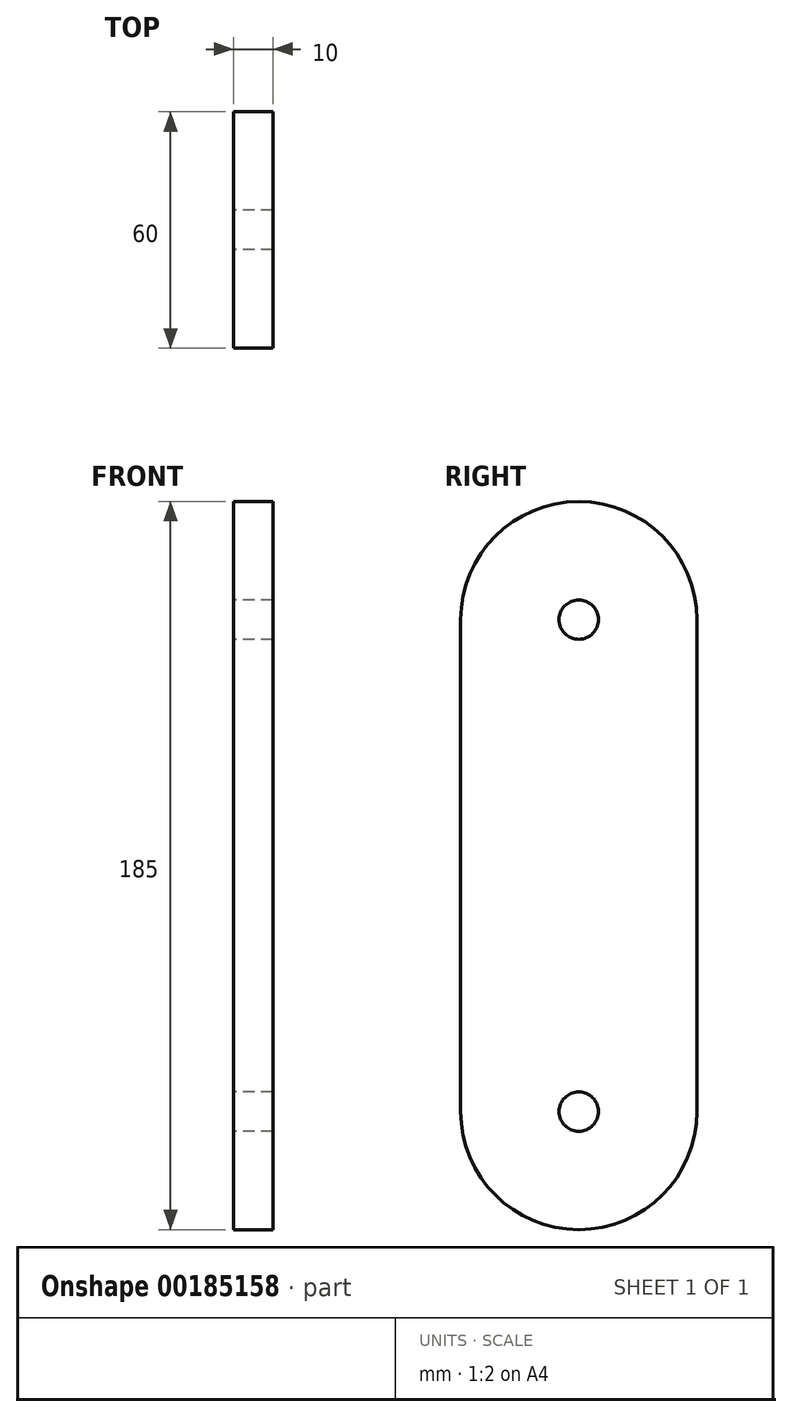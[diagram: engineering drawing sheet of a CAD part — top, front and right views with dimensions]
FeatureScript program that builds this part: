
annotation { "Feature Type Name" : "Feature", "Feature Type Description" : "" }
export const myFeature = defineFeature(function(context is Context, id is Id, definition is map)
    precondition{}
    {
        {
            var Q0;
            Q0=qCreatedBy(makeId("Right.planeOp"),FACE);
            var sketch = newSketch(context, id + "F0", { "sketchPlane" : qUnion([Q0])});
            skCircle(sketch, "E0", {"center": v(0, 0) * mm, "radius": 5 * mm});
            skArc(sketch, "E1", {"start": v(-30, 0) * mm, "mid": v(0, -30) * mm, "end": v(30, 0) * mm});
            skLineSegment(sketch, "E2", {"start": v(0, 0) * mm, "end": v(5, 0) * mm});
            skLineSegment(sketch, "E3", {"start": v(-30, 0) * mm, "end": v(-30, 125) * mm});
            skLineSegment(sketch, "E4", {"start": v(30, 0) * mm, "end": v(30, 125) * mm});
            skCircle(sketch, "E5", {"center": v(0, 125) * mm, "radius": 5 * mm});
            skArc(sketch, "E6", {"start": v(30, 125) * mm, "mid": v(0, 155) * mm, "end": v(-30, 125) * mm});
            skLineSegment(sketch, "E7", {"start": v(0, 0) * mm, "end": v(30, 0) * mm});
            skLineSegment(sketch, "E8", {"start": v(0, 125) * mm, "end": v(30, 125) * mm});
            skLineSegment(sketch, "E9", {"start": v(-30, 125) * mm, "end": v(30, 125) * mm});
            skSolve(sketch);
        }
        {
            var Q0;
            Q0=qSketchRegion(id+"F0",true);
            extrude(context, id + "F1", {"entities" : qUnion([Q0]), "depth" : 10 * mm});
        }
    });
